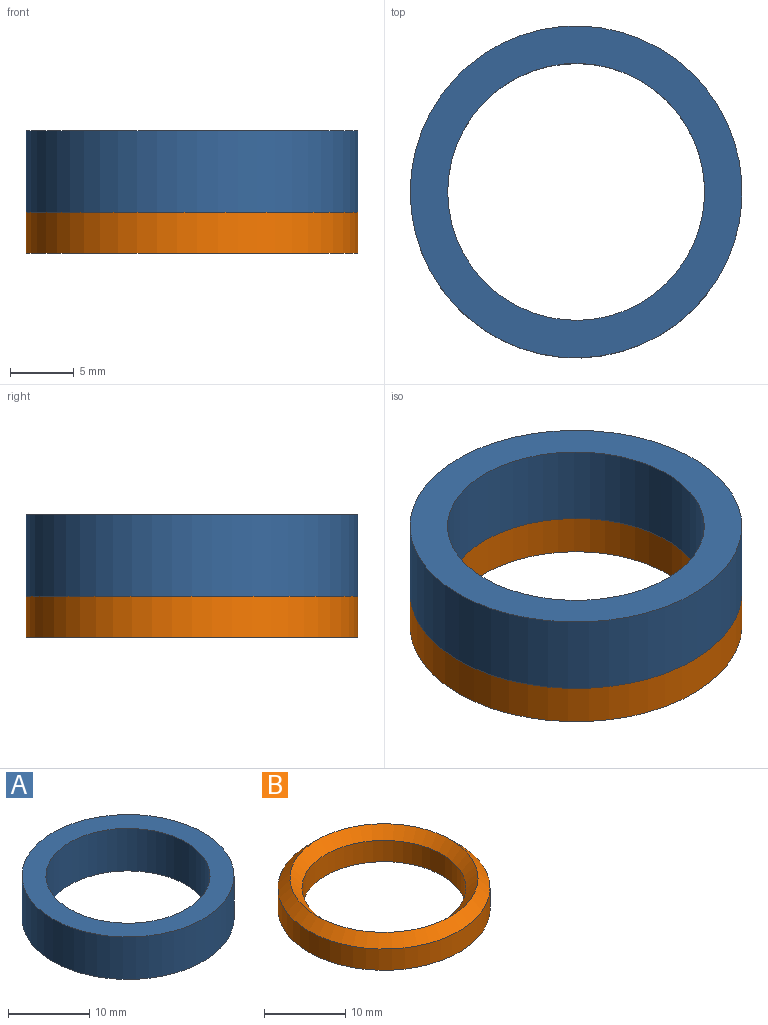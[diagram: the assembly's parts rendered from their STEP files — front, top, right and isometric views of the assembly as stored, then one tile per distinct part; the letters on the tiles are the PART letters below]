
ASSEMBLY  parts=2 mates=1
PART A: 5 faces, bbox 26.1x26.1x6.4 mm
  f0: cylinder r=13.05mm len=26.1mm, axis (0,0,-1), area 524.8mm2, adj f1,f4
  f1: cone r=13.05mm half-angle=30deg, axis (0,0,-1), area 228.2mm2, adj f0,f2
  f2: cone r=10.1mm half-angle=30deg, axis (0,0,1), area 200.9mm2, adj f1,f3
  f3: cylinder r=10.1mm len=20.2mm, axis (0,0,-1), area 406.1mm2, adj f2,f4
  f4: plane 26.1x26.1mm, normal (0,0,1), area 214.5mm2, adj f0,f3
PART B: 5 faces, bbox 26.1x26.1x4.7 mm
  f0: cylinder r=13.05mm len=26.1mm, axis (0,0,-1), area 262.4mm2, adj f1,f4
  f1: plane 26.1x26.1mm, normal (0,0,-1), area 214.5mm2, adj f0,f2
  f2: cylinder r=10.1mm len=20.2mm, axis (0,0,-1), area 203.1mm2, adj f1,f3
  f3: cone r=10.1mm half-angle=45deg, axis (0,0,1), area 142mm2, adj f2,f4
  f4: cone r=13.05mm half-angle=45deg, axis (0,0,-1), area 161.4mm2, adj f0,f3
PLACE A t=(-11.88,0.01,3.89)mm
PLACE B t=(-11.88,0.01,3.89)mm
MATE fastened B.f0 <-> A.f0  axis (0,0,-1) through (-11.88,0.01,7.09)mm
